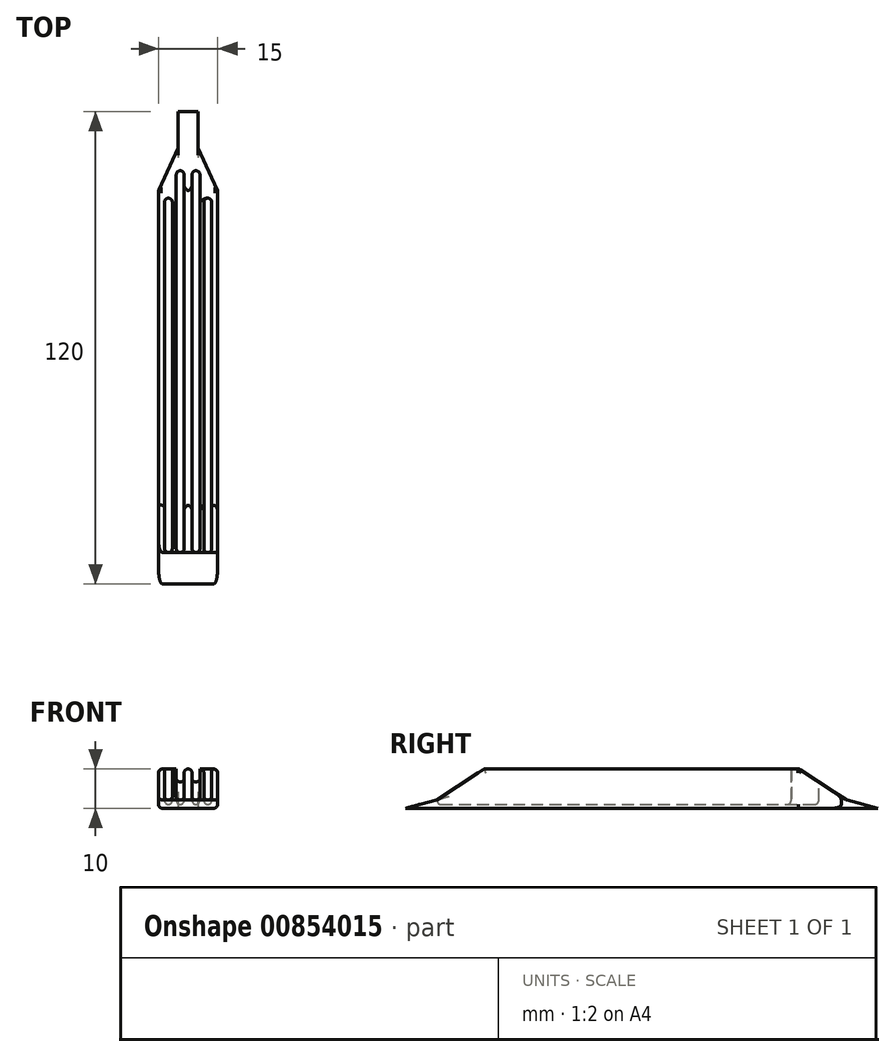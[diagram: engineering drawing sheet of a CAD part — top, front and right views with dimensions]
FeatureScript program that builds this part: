
annotation { "Feature Type Name" : "Feature", "Feature Type Description" : "" }
export const myFeature = defineFeature(function(context is Context, id is Id, definition is map)
    precondition{}
    {
        {
            var Q0;
            Q0=qCreatedBy(makeId("Right.planeOp"),FACE);
            var sketch = newSketch(context, id + "F0", { "sketchPlane" : qUnion([Q0])});
            skLineSegment(sketch, "E0.bottom", {"start": v(-60, 0) * mm, "end": v(60, 0) * mm});
            skLineSegment(sketch, "E0.top", {"start": v(-60, 10) * mm, "end": v(60, 10) * mm});
            skLineSegment(sketch, "E0.left", {"start": v(-60, 0) * mm, "end": v(-60, 10) * mm});
            skLineSegment(sketch, "E0.right", {"start": v(60, 0) * mm, "end": v(60, 10) * mm});
            skLineSegment(sketch, "E1", {"start": v(-60, 0) * mm, "end": v(-52, 2.14) * mm});
            skLineSegment(sketch, "E2", {"start": v(-52, 2.14) * mm, "end": v(-40, 10) * mm});
            skLineSegment(sketch, "E3.MirrorCS", {"start": v(52, 2.14) * mm, "end": v(40, 10) * mm});
            skLineSegment(sketch, "E4.MirrorCS", {"start": v(60, 0) * mm, "end": v(52, 2.14) * mm});
            skSolve(sketch);
        }
        {
            var Q0;
            Q0=makeQuery(id+"F0.imprint","IMPRINT",FACE,{"disambiguationData":[TD([[makeQuery(id+"F0.imprint","IMPRINT",EDGE,{"derivedFrom":sQuery(id+"F0.wireOp",EDGE,"E0.bottom")}),1.0]])]});
            extrude(context, id + "F1", {"entities" : qUnion([Q0]), "endBound" : BoundingType.SYMMETRIC, "depth" : 15 * mm, "offsetDistance" : 25 * mm});
        }
        {
            var Q0;
            Q0=makeQuery(id+"F1.opExtrude","SWEPT_FACE",FACE,{"disambiguationData":[OSD([sQuery(id+"F0.wireOp",EDGE,"E0.top")])]});
            var sketch = newSketch(context, id + "F2", { "sketchPlane" : qUnion([Q0])});
            skLineSegment(sketch, "E5.0", {"start": v(7.5, 60) * mm, "end": v(-7.5, 60) * mm});
            skLineSegment(sketch, "E6", {"start": v(-2.5, 60) * mm, "end": v(-2.5, 50.72) * mm});
            skLineSegment(sketch, "E7", {"start": v(-7.5, 60) * mm, "end": v(-7.5, 40) * mm});
            skLineSegment(sketch, "E8", {"start": v(-7.5, 40) * mm, "end": v(-2.5, 50.72) * mm});
            skLineSegment(sketch, "E9.MirrorCS", {"start": v(2.5, 60) * mm, "end": v(2.5, 50.72) * mm});
            skLineSegment(sketch, "E10.MirrorCS", {"start": v(7.5, 40) * mm, "end": v(2.5, 50.72) * mm});
            skLineSegment(sketch, "E11.MirrorCS", {"start": v(7.5, 60) * mm, "end": v(7.5, 40) * mm});
            skSolve(sketch);
        }
        {
            var Q0;
            {var subQ2=sQuery(id+"F2.wireOp",EDGE,"E6");Q0=makeQuery(id+"F2.imprint","IMPRINT",FACE,{"disambiguationData":[TD([[makeQuery(id+"F2.imprint","IMPRINT",EDGE,{"derivedFrom":subQ2}),-1.0]])]});}
            var Q1;
            {var subQ2=sQuery(id+"F2.wireOp",EDGE,"E9.MirrorCS");Q1=makeQuery(id+"F2.imprint","IMPRINT",FACE,{"disambiguationData":[TD([[makeQuery(id+"F2.imprint","IMPRINT",EDGE,{"derivedFrom":subQ2}),1.0]])]});}
            extrude(context, id + "F3", {"entities" : qUnion([Q0, Q1]), "operationType" : NewBodyOperationType.REMOVE, "endBound" : BoundingType.SYMMETRIC, "oppositeDirection" : true, "depth" : 50 * mm, "offsetDistance" : 25 * mm});
        }
        {
            var Q0;
            Q0=makeQuery(id+"F1.opExtrude","SWEPT_FACE",FACE,{"disambiguationData":[OSD([sQuery(id+"F0.wireOp",EDGE,"E0.top")])]});
            var sketch = newSketch(context, id + "F4", { "sketchPlane" : qUnion([Q0])});
            skLineSegment(sketch, "E12.bottom", {"start": v(-6, 38) * mm, "end": v(-4, 38) * mm});
            skLineSegment(sketch, "E12.top", {"start": v(-6, -52) * mm, "end": v(-4, -52) * mm});
            skLineSegment(sketch, "E12.left", {"start": v(-6, 38) * mm, "end": v(-6, -52) * mm});
            skLineSegment(sketch, "E12.right", {"start": v(-4, 38) * mm, "end": v(-4, -52) * mm});
            skLineSegment(sketch, "E13.MirrorCS", {"start": v(6, 38) * mm, "end": v(6, -52) * mm});
            skLineSegment(sketch, "E14.MirrorCS", {"start": v(4, 38) * mm, "end": v(4, -52) * mm});
            skLineSegment(sketch, "E15.MirrorCS", {"start": v(6, 38) * mm, "end": v(4, 38) * mm});
            skLineSegment(sketch, "E16.MirrorCS", {"start": v(6, -52) * mm, "end": v(4, -52) * mm});
            skLineSegment(sketch, "E17.bottom", {"start": v(-3, 45) * mm, "end": v(-1, 45) * mm});
            skLineSegment(sketch, "E17.top", {"start": v(-3, -52) * mm, "end": v(-1, -52) * mm});
            skLineSegment(sketch, "E17.left", {"start": v(-3, 45) * mm, "end": v(-3, -52) * mm});
            skLineSegment(sketch, "E17.right", {"start": v(-1, 45) * mm, "end": v(-1, -52) * mm});
            skLineSegment(sketch, "E18.MirrorCS", {"start": v(1, 45) * mm, "end": v(1, -52) * mm});
            skLineSegment(sketch, "E19.MirrorCS", {"start": v(3, 45) * mm, "end": v(1, 45) * mm});
            skLineSegment(sketch, "E20.MirrorCS", {"start": v(3, 45) * mm, "end": v(3, -52) * mm});
            skLineSegment(sketch, "E21.MirrorCS", {"start": v(3, -52) * mm, "end": v(1, -52) * mm});
            skSolve(sketch);
        }
        {
            var Q0;
            {var subQ0=sQuery(id+"F4.wireOp",EDGE,"E12.bottom");Q0=makeQuery(id+"F4.imprint","IMPRINT",FACE,{"disambiguationData":[TD([[makeQuery(id+"F4.imprint","IMPRINT",EDGE,{"derivedFrom":subQ0}),-1.0]])]});}
            var Q1;
            {var subQ0=sQuery(id+"F4.wireOp",EDGE,"E17.left");var subQ1=sQuery(id+"F0.wireOp",EDGE,"E0.top");var subQ2=makeQuery(id+"F1.opExtrude","SWEPT_EDGE",EDGE,{"disambiguationData":[OSD([subQ1,sQuery(id+"F0.wireOp",EDGE,"E3.MirrorCS")])]});var subQ3=makeQuery(id+"F4.imprint","INTERSECT",VERTEX,{"derivedFrom":[subQ2,subQ0]});Q1=makeQuery(id+"F4.imprint","IMPRINT",FACE,{"disambiguationData":[TD([[makeQuery(id+"F4.imprint","IMPRINT",EDGE,{"disambiguationData":[TD([[subQ3,-1.0]])],"derivedFrom":subQ0}),1.0]])]});}
            var Q2;
            {var subQ0=sQuery(id+"F4.wireOp",EDGE,"E17.bottom");Q2=makeQuery(id+"F4.imprint","IMPRINT",FACE,{"disambiguationData":[TD([[makeQuery(id+"F4.imprint","IMPRINT",EDGE,{"derivedFrom":subQ0}),-1.0]])]});}
            var Q3;
            {var subQ0=sQuery(id+"F4.wireOp",EDGE,"E19.MirrorCS");Q3=makeQuery(id+"F4.imprint","IMPRINT",FACE,{"disambiguationData":[TD([[makeQuery(id+"F4.imprint","IMPRINT",EDGE,{"derivedFrom":subQ0}),1.0]])]});}
            var Q4;
            {var subQ0=sQuery(id+"F4.wireOp",EDGE,"E18.MirrorCS");var subQ1=sQuery(id+"F0.wireOp",EDGE,"E0.top");var subQ2=makeQuery(id+"F1.opExtrude","SWEPT_EDGE",EDGE,{"disambiguationData":[OSD([subQ1,sQuery(id+"F0.wireOp",EDGE,"E3.MirrorCS")])]});var subQ3=makeQuery(id+"F4.imprint","INTERSECT",VERTEX,{"derivedFrom":[subQ2,subQ0]});Q4=makeQuery(id+"F4.imprint","IMPRINT",FACE,{"disambiguationData":[TD([[makeQuery(id+"F4.imprint","IMPRINT",EDGE,{"disambiguationData":[TD([[subQ3,-1.0]])],"derivedFrom":subQ0}),1.0]])]});}
            var Q5;
            {var subQ0=sQuery(id+"F4.wireOp",EDGE,"E15.MirrorCS");Q5=makeQuery(id+"F4.imprint","IMPRINT",FACE,{"disambiguationData":[TD([[makeQuery(id+"F4.imprint","IMPRINT",EDGE,{"derivedFrom":subQ0}),1.0]])]});}
            var Q6;
            {var subQ0=sQuery(id+"F4.wireOp",EDGE,"E16.MirrorCS");Q6=makeQuery(id+"F4.imprint","IMPRINT",FACE,{"disambiguationData":[TD([[makeQuery(id+"F4.imprint","IMPRINT",EDGE,{"derivedFrom":subQ0}),-1.0]])]});}
            var Q7;
            {var subQ0=sQuery(id+"F4.wireOp",EDGE,"E21.MirrorCS");Q7=makeQuery(id+"F4.imprint","IMPRINT",FACE,{"disambiguationData":[TD([[makeQuery(id+"F4.imprint","IMPRINT",EDGE,{"derivedFrom":subQ0}),-1.0]])]});}
            var Q8;
            {var subQ0=sQuery(id+"F4.wireOp",EDGE,"E17.top");Q8=makeQuery(id+"F4.imprint","IMPRINT",FACE,{"disambiguationData":[TD([[makeQuery(id+"F4.imprint","IMPRINT",EDGE,{"derivedFrom":subQ0}),1.0]])]});}
            var Q9;
            {var subQ0=sQuery(id+"F4.wireOp",EDGE,"E12.top");Q9=makeQuery(id+"F4.imprint","IMPRINT",FACE,{"disambiguationData":[TD([[makeQuery(id+"F4.imprint","IMPRINT",EDGE,{"derivedFrom":subQ0}),1.0]])]});}
            extrude(context, id + "F5", {"entities" : qUnion([Q0, Q1, Q2, Q3, Q4, Q5, Q6, Q7, Q8, Q9]), "operationType" : NewBodyOperationType.REMOVE, "oppositeDirection" : true, "depth" : 9 * mm, "offsetDistance" : 25 * mm});
        }
        {
            var Q0;
            Q0=makeQuery(id+"F3.boolean.opBoolean","INTERSECT",EDGE,{"derivedFrom":[makeQuery(id+"F1.opExtrude","SWEPT_FACE",FACE,{"disambiguationData":[OSD([sQuery(id+"F0.wireOp",EDGE,"E3.MirrorCS")])]}),makeQuery(id+"F3.opExtrude","SWEPT_FACE",FACE,{"disambiguationData":[OSD([sQuery(id+"F2.wireOp",EDGE,"E8")])]})]});
            var Q1;
            Q1=makeQuery(id+"F1.opExtrude","CAP_EDGE",EDGE,{"disambiguationData":[OSD([sQuery(id+"F0.wireOp",EDGE,"E0.top")])],"isStart":true});
            var Q2;
            Q2=makeQuery(id+"F1.opExtrude","CAP_EDGE",EDGE,{"disambiguationData":[OSD([sQuery(id+"F0.wireOp",EDGE,"E2")])],"isStart":true});
            var Q3;
            Q3=makeQuery(id+"F1.opExtrude","CAP_EDGE",EDGE,{"disambiguationData":[OSD([sQuery(id+"F0.wireOp",EDGE,"E0.bottom")])],"isStart":true});
            var Q4;
            Q4=makeQuery(id+"F1.opExtrude","CAP_EDGE",EDGE,{"disambiguationData":[OSD([sQuery(id+"F0.wireOp",EDGE,"E0.bottom")])],"isStart":false});
            var Q5;
            Q5=makeQuery(id+"F5.boolean.opBoolean","COPY",EDGE,{"derivedFrom":makeQuery(id+"F5.opExtrude","CAP_EDGE",EDGE,{"disambiguationData":[OSD([sQuery(id+"F4.wireOp",EDGE,"E17.right")])],"isStart":true})});
            var Q6;
            Q6=makeQuery(id+"F5.boolean.opBoolean","COPY",EDGE,{"derivedFrom":makeQuery(id+"F5.opExtrude","CAP_EDGE",EDGE,{"disambiguationData":[OSD([sQuery(id+"F4.wireOp",EDGE,"E18.MirrorCS")])],"isStart":true})});
            var Q7;
            Q7=makeQuery(id+"F1.opExtrude","CAP_EDGE",EDGE,{"disambiguationData":[OSD([sQuery(id+"F0.wireOp",EDGE,"E0.top")])],"isStart":false});
            var Q8;
            Q8=makeQuery(id+"F5.boolean.opBoolean","COPY",EDGE,{"derivedFrom":makeQuery(id+"F5.opExtrude","CAP_EDGE",EDGE,{"disambiguationData":[OSD([sQuery(id+"F4.wireOp",EDGE,"E12.right")])],"isStart":true})});
            var Q9;
            Q9=makeQuery(id+"F5.boolean.opBoolean","COPY",EDGE,{"derivedFrom":makeQuery(id+"F5.opExtrude","CAP_EDGE",EDGE,{"disambiguationData":[OSD([sQuery(id+"F4.wireOp",EDGE,"E14.MirrorCS")])],"isStart":true})});
            var Q10;
            Q10=makeQuery(id+"F5.boolean.opBoolean","COPY",EDGE,{"derivedFrom":makeQuery(id+"F5.opExtrude","CAP_EDGE",EDGE,{"disambiguationData":[OSD([sQuery(id+"F4.wireOp",EDGE,"E17.right")])],"isStart":false})});
            var Q11;
            Q11=makeQuery(id+"F5.boolean.opBoolean","COPY",EDGE,{"derivedFrom":makeQuery(id+"F5.opExtrude","CAP_EDGE",EDGE,{"disambiguationData":[OSD([sQuery(id+"F4.wireOp",EDGE,"E18.MirrorCS")])],"isStart":false})});
            var Q12;
            Q12=makeQuery(id+"F5.boolean.opBoolean","COPY",EDGE,{"derivedFrom":makeQuery(id+"F5.opExtrude","CAP_EDGE",EDGE,{"disambiguationData":[OSD([sQuery(id+"F4.wireOp",EDGE,"E12.right")])],"isStart":false})});
            var Q13;
            Q13=makeQuery(id+"F5.boolean.opBoolean","COPY",EDGE,{"derivedFrom":makeQuery(id+"F5.opExtrude","CAP_EDGE",EDGE,{"disambiguationData":[OSD([sQuery(id+"F4.wireOp",EDGE,"E12.left")])],"isStart":false})});
            var Q14;
            Q14=makeQuery(id+"F5.boolean.opBoolean","COPY",EDGE,{"derivedFrom":makeQuery(id+"F5.opExtrude","CAP_EDGE",EDGE,{"disambiguationData":[OSD([sQuery(id+"F4.wireOp",EDGE,"E13.MirrorCS")])],"isStart":false})});
            var Q15;
            Q15=makeQuery(id+"F5.boolean.opBoolean","COPY",EDGE,{"derivedFrom":makeQuery(id+"F5.opExtrude","CAP_EDGE",EDGE,{"disambiguationData":[OSD([sQuery(id+"F4.wireOp",EDGE,"E14.MirrorCS")])],"isStart":false})});
            var Q16;
            Q16=makeQuery(id+"F5.boolean.opBoolean","COPY",EDGE,{"derivedFrom":makeQuery(id+"F5.opExtrude","CAP_EDGE",EDGE,{"disambiguationData":[OSD([sQuery(id+"F4.wireOp",EDGE,"E17.left")])],"isStart":false})});
            var Q17;
            Q17=makeQuery(id+"F3.boolean.opBoolean","INTERSECT",EDGE,{"derivedFrom":[makeQuery(id+"F1.opExtrude","SWEPT_FACE",FACE,{"disambiguationData":[OSD([sQuery(id+"F0.wireOp",EDGE,"E3.MirrorCS")])]}),makeQuery(id+"F3.opExtrude","SWEPT_FACE",FACE,{"disambiguationData":[OSD([sQuery(id+"F2.wireOp",EDGE,"E10.MirrorCS")])]})]});
            fillet(context, id + "F6", {"entities" : qUnion([Q0, Q1, Q2, Q3, Q4, Q5, Q6, Q7, Q8, Q9, Q10, Q11, Q12, Q13, Q14, Q15, Q16, Q17]), "radius" : 1 * mm, "tangentPropagation" : true, "allowEdgeOverflow" : false});
        }
        {
            var Q0;
            Q0=makeQuery(id+"F5.boolean.opBoolean","COPY",EDGE,{"derivedFrom":makeQuery(id+"F5.opExtrude","CAP_EDGE",EDGE,{"disambiguationData":[OSD([sQuery(id+"F4.wireOp",EDGE,"E20.MirrorCS")])],"isStart":false})});
            var Q1;
            {var subQ0=sQuery(id+"F4.wireOp",EDGE,"E14.MirrorCS");Q1=makeQuery(id+"F6.opFillet","BLEND_EDGE",EDGE,{"blendedFrom":[makeQuery(id+"F5.boolean.opBoolean","COPY",EDGE,{"derivedFrom":makeQuery(id+"F5.opExtrude","CAP_EDGE",EDGE,{"disambiguationData":[OSD([subQ0])],"isStart":false})}),makeQuery(id+"F5.boolean.opBoolean","COPY",FACE,{"derivedFrom":makeQuery(id+"F5.opExtrude","SWEPT_FACE",FACE,{"disambiguationData":[OSD([subQ0])]})})],"blendedInto":[makeQuery(id+"F5.boolean.opBoolean","COPY",FACE,{"derivedFrom":makeQuery(id+"F5.opExtrude","SWEPT_FACE",FACE,{"disambiguationData":[OSD([subQ0])]})})]});}
            fillet(context, id + "F7", {"entities" : qUnion([Q0, Q1]), "radius" : 1 * mm, "tangentPropagation" : true, "allowEdgeOverflow" : false});
        }
        {
            var Q0;
            Q0=makeQuery(id+"F6.opFillet","BLEND_EDGE",EDGE,{"blendedFrom":[makeQuery(id+"F5.boolean.opBoolean","COPY",EDGE,{"derivedFrom":makeQuery(id+"F5.opExtrude","CAP_EDGE",EDGE,{"disambiguationData":[OSD([sQuery(id+"F4.wireOp",EDGE,"E12.left")])],"isStart":false})}),makeQuery(id+"F5.boolean.opBoolean","COPY",FACE,{"derivedFrom":makeQuery(id+"F5.opExtrude","SWEPT_FACE",FACE,{"disambiguationData":[OSD([sQuery(id+"F4.wireOp",EDGE,"E12.top")])]})})],"blendedInto":[makeQuery(id+"F5.boolean.opBoolean","COPY",FACE,{"derivedFrom":makeQuery(id+"F5.opExtrude","SWEPT_FACE",FACE,{"disambiguationData":[OSD([sQuery(id+"F4.wireOp",EDGE,"E12.top")])]})})]});
            var Q1;
            Q1=makeQuery(id+"F6.opFillet","BLEND_EDGE",EDGE,{"blendedFrom":[makeQuery(id+"F5.boolean.opBoolean","COPY",EDGE,{"derivedFrom":makeQuery(id+"F5.opExtrude","CAP_EDGE",EDGE,{"disambiguationData":[OSD([sQuery(id+"F4.wireOp",EDGE,"E17.left")])],"isStart":false})}),makeQuery(id+"F5.boolean.opBoolean","COPY",FACE,{"derivedFrom":makeQuery(id+"F5.opExtrude","SWEPT_FACE",FACE,{"disambiguationData":[OSD([sQuery(id+"F4.wireOp",EDGE,"E17.top")])]})})],"blendedInto":[makeQuery(id+"F5.boolean.opBoolean","COPY",FACE,{"derivedFrom":makeQuery(id+"F5.opExtrude","SWEPT_FACE",FACE,{"disambiguationData":[OSD([sQuery(id+"F4.wireOp",EDGE,"E17.top")])]})})]});
            var Q2;
            Q2=makeQuery(id+"F6.opFillet","BLEND_EDGE",EDGE,{"blendedFrom":[makeQuery(id+"F5.boolean.opBoolean","COPY",EDGE,{"derivedFrom":makeQuery(id+"F5.opExtrude","CAP_EDGE",EDGE,{"disambiguationData":[OSD([sQuery(id+"F4.wireOp",EDGE,"E18.MirrorCS")])],"isStart":false})}),makeQuery(id+"F5.boolean.opBoolean","COPY",FACE,{"derivedFrom":makeQuery(id+"F5.opExtrude","SWEPT_FACE",FACE,{"disambiguationData":[OSD([sQuery(id+"F4.wireOp",EDGE,"E21.MirrorCS")])]})})],"blendedInto":[makeQuery(id+"F5.boolean.opBoolean","COPY",FACE,{"derivedFrom":makeQuery(id+"F5.opExtrude","SWEPT_FACE",FACE,{"disambiguationData":[OSD([sQuery(id+"F4.wireOp",EDGE,"E21.MirrorCS")])]})})]});
            var Q3;
            Q3=makeQuery(id+"F6.opFillet","BLEND_EDGE",EDGE,{"blendedFrom":[makeQuery(id+"F5.boolean.opBoolean","COPY",EDGE,{"derivedFrom":makeQuery(id+"F5.opExtrude","CAP_EDGE",EDGE,{"disambiguationData":[OSD([sQuery(id+"F4.wireOp",EDGE,"E13.MirrorCS")])],"isStart":false})}),makeQuery(id+"F5.boolean.opBoolean","COPY",FACE,{"derivedFrom":makeQuery(id+"F5.opExtrude","SWEPT_FACE",FACE,{"disambiguationData":[OSD([sQuery(id+"F4.wireOp",EDGE,"E16.MirrorCS")])]})})],"blendedInto":[makeQuery(id+"F5.boolean.opBoolean","COPY",FACE,{"derivedFrom":makeQuery(id+"F5.opExtrude","SWEPT_FACE",FACE,{"disambiguationData":[OSD([sQuery(id+"F4.wireOp",EDGE,"E16.MirrorCS")])]})})]});
            var Q4;
            Q4=makeQuery(id+"F6.opFillet","BLEND_EDGE",EDGE,{"blendedFrom":[makeQuery(id+"F5.boolean.opBoolean","COPY",EDGE,{"derivedFrom":makeQuery(id+"F5.opExtrude","CAP_EDGE",EDGE,{"disambiguationData":[OSD([sQuery(id+"F4.wireOp",EDGE,"E17.left")])],"isStart":false})}),makeQuery(id+"F5.boolean.opBoolean","COPY",FACE,{"derivedFrom":makeQuery(id+"F5.opExtrude","SWEPT_FACE",FACE,{"disambiguationData":[OSD([sQuery(id+"F4.wireOp",EDGE,"E17.bottom")])]})})],"blendedInto":[makeQuery(id+"F5.boolean.opBoolean","COPY",FACE,{"derivedFrom":makeQuery(id+"F5.opExtrude","SWEPT_FACE",FACE,{"disambiguationData":[OSD([sQuery(id+"F4.wireOp",EDGE,"E17.bottom")])]})})]});
            var Q5;
            Q5=makeQuery(id+"F6.opFillet","BLEND_EDGE",EDGE,{"blendedFrom":[makeQuery(id+"F5.boolean.opBoolean","COPY",EDGE,{"derivedFrom":makeQuery(id+"F5.opExtrude","CAP_EDGE",EDGE,{"disambiguationData":[OSD([sQuery(id+"F4.wireOp",EDGE,"E12.left")])],"isStart":false})}),makeQuery(id+"F5.boolean.opBoolean","COPY",FACE,{"derivedFrom":makeQuery(id+"F5.opExtrude","SWEPT_FACE",FACE,{"disambiguationData":[OSD([sQuery(id+"F4.wireOp",EDGE,"E12.bottom")])]})})],"blendedInto":[makeQuery(id+"F5.boolean.opBoolean","COPY",FACE,{"derivedFrom":makeQuery(id+"F5.opExtrude","SWEPT_FACE",FACE,{"disambiguationData":[OSD([sQuery(id+"F4.wireOp",EDGE,"E12.bottom")])]})})]});
            var Q6;
            Q6=makeQuery(id+"F7.opFillet","BLEND_EDGE",EDGE,{"blendedFrom":[makeQuery(id+"F5.boolean.opBoolean","COPY",EDGE,{"derivedFrom":makeQuery(id+"F5.opExtrude","CAP_EDGE",EDGE,{"disambiguationData":[OSD([sQuery(id+"F4.wireOp",EDGE,"E20.MirrorCS")])],"isStart":false})}),makeQuery(id+"F5.boolean.opBoolean","COPY",FACE,{"derivedFrom":makeQuery(id+"F5.opExtrude","SWEPT_FACE",FACE,{"disambiguationData":[OSD([sQuery(id+"F4.wireOp",EDGE,"E19.MirrorCS")])]})})],"blendedInto":[makeQuery(id+"F5.boolean.opBoolean","COPY",FACE,{"derivedFrom":makeQuery(id+"F5.opExtrude","SWEPT_FACE",FACE,{"disambiguationData":[OSD([sQuery(id+"F4.wireOp",EDGE,"E19.MirrorCS")])]})})]});
            var Q7;
            Q7=makeQuery(id+"F6.opFillet","BLEND_EDGE",EDGE,{"blendedFrom":[makeQuery(id+"F5.boolean.opBoolean","COPY",EDGE,{"derivedFrom":makeQuery(id+"F5.opExtrude","CAP_EDGE",EDGE,{"disambiguationData":[OSD([sQuery(id+"F4.wireOp",EDGE,"E13.MirrorCS")])],"isStart":false})}),makeQuery(id+"F5.boolean.opBoolean","COPY",FACE,{"derivedFrom":makeQuery(id+"F5.opExtrude","SWEPT_FACE",FACE,{"disambiguationData":[OSD([sQuery(id+"F4.wireOp",EDGE,"E15.MirrorCS")])]})})],"blendedInto":[makeQuery(id+"F5.boolean.opBoolean","COPY",FACE,{"derivedFrom":makeQuery(id+"F5.opExtrude","SWEPT_FACE",FACE,{"disambiguationData":[OSD([sQuery(id+"F4.wireOp",EDGE,"E15.MirrorCS")])]})})]});
            var Q8;
            Q8=makeQuery(id+"F1.opExtrude","SWEPT_EDGE",EDGE,{"disambiguationData":[OSD([sQuery(id+"F0.wireOp",EDGE,"E3.MirrorCS"),sQuery(id+"F0.wireOp",EDGE,"E4.MirrorCS")])]});
            var Q9;
            {var subQ0=sQuery(id+"F0.wireOp",EDGE,"E3.MirrorCS");var subQ1=sQuery(id+"F0.wireOp",EDGE,"E0.top");Q9=makeQuery(id+"F5.boolean.opBoolean","SPLIT",EDGE,{"disambiguationData":[TD([makeQuery(id+"F3.boolean.opBoolean","COPY",FACE,{"derivedFrom":makeQuery(id+"F3.opExtrude","SWEPT_FACE",FACE,{"disambiguationData":[OSD([sQuery(id+"F2.wireOp",EDGE,"E10.MirrorCS")])]})})])],"derivedFrom":makeQuery(id+"F1.opExtrude","SWEPT_EDGE",EDGE,{"disambiguationData":[OSD([subQ1,subQ0])]})});}
            var Q10;
            {var subQ0=sQuery(id+"F0.wireOp",EDGE,"E3.MirrorCS");var subQ1=sQuery(id+"F0.wireOp",EDGE,"E0.top");Q10=makeQuery(id+"F5.boolean.opBoolean","SPLIT",EDGE,{"disambiguationData":[TD([makeQuery(id+"F3.boolean.opBoolean","COPY",FACE,{"derivedFrom":makeQuery(id+"F3.opExtrude","SWEPT_FACE",FACE,{"disambiguationData":[OSD([sQuery(id+"F2.wireOp",EDGE,"E8")])]})})])],"derivedFrom":makeQuery(id+"F1.opExtrude","SWEPT_EDGE",EDGE,{"disambiguationData":[OSD([subQ1,subQ0])]})});}
            fillet(context, id + "F8", {"entities" : qUnion([Q0, Q1, Q2, Q3, Q4, Q5, Q6, Q7, Q8, Q9, Q10]), "radius" : 1 * mm, "tangentPropagation" : true, "allowEdgeOverflow" : false});
        }
    });
